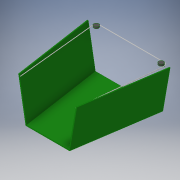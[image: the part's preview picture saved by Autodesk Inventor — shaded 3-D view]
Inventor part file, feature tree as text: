
AUTODESK INVENTOR PART (.ipt)
format: ipt  version: 2019 (Build 230136000, 136)  size: 192,512 bytes
history: native  units: in
note: dims shown in document units (in); Inventor stores cm internally (conversion verified against a paired STEP export)
features: sketch x6, plane x3, extrude x1, sweep x1, loft x1
ambient origin geometry x8: Origin, YZ Plane, XZ Plane, XY Plane, X Axis, Y Axis, Z Axis, Center Point
bodies: Solid1 (feature_tree)
feature tree (12):
  sketch  "Sketch1"  dims[d0=0.1969in d1=0.1969in]
  sketch  "Sketch2"  dims[d2=0.1969in d3=0.0in]
  plane  "Work Plane1"
  plane  "Work Plane2"
  extrude  "Extrusion1"  Depth=0.1969in
  sketch  "Sketch6"  dims[d7=0.5497in]
  plane  "Work Plane3"
  sweep  "Sweep1"
  loft  "Loft2"
  sketch  "Sketch5"  dims[d6=9.8425in]
  sketch  "Sketch8"  dims[d8=0.5497in d9=0.1969in d10=0.1969in d11=19.685in d12=0.1969in d13=0.1969in d14=0.1969in d15=0.0in d16=0.0in d17=13.7795in d18=9.8425in d19=0.5497in d20=0.5497in d21=0.1969in d22=0.1969in d23=0.1969in d24=1.1811in d25=15.748in d26=0.5497in d34=1.1811in d35=1.1811in d36=0.3937in d37=0.0in d40=0.1575in d41=0.0in d42=0.0in d43=0.0in d44=90.0deg d45=0.0in d46=90.0deg d47=0.3937in d48=0.3937in d49=0.0in d50=0.9843in d51=0.7874in d52=19.685in d53=13.3858in]
  sketch  "Sketch4"  dims[d4=0.0in d5=19.685in]
